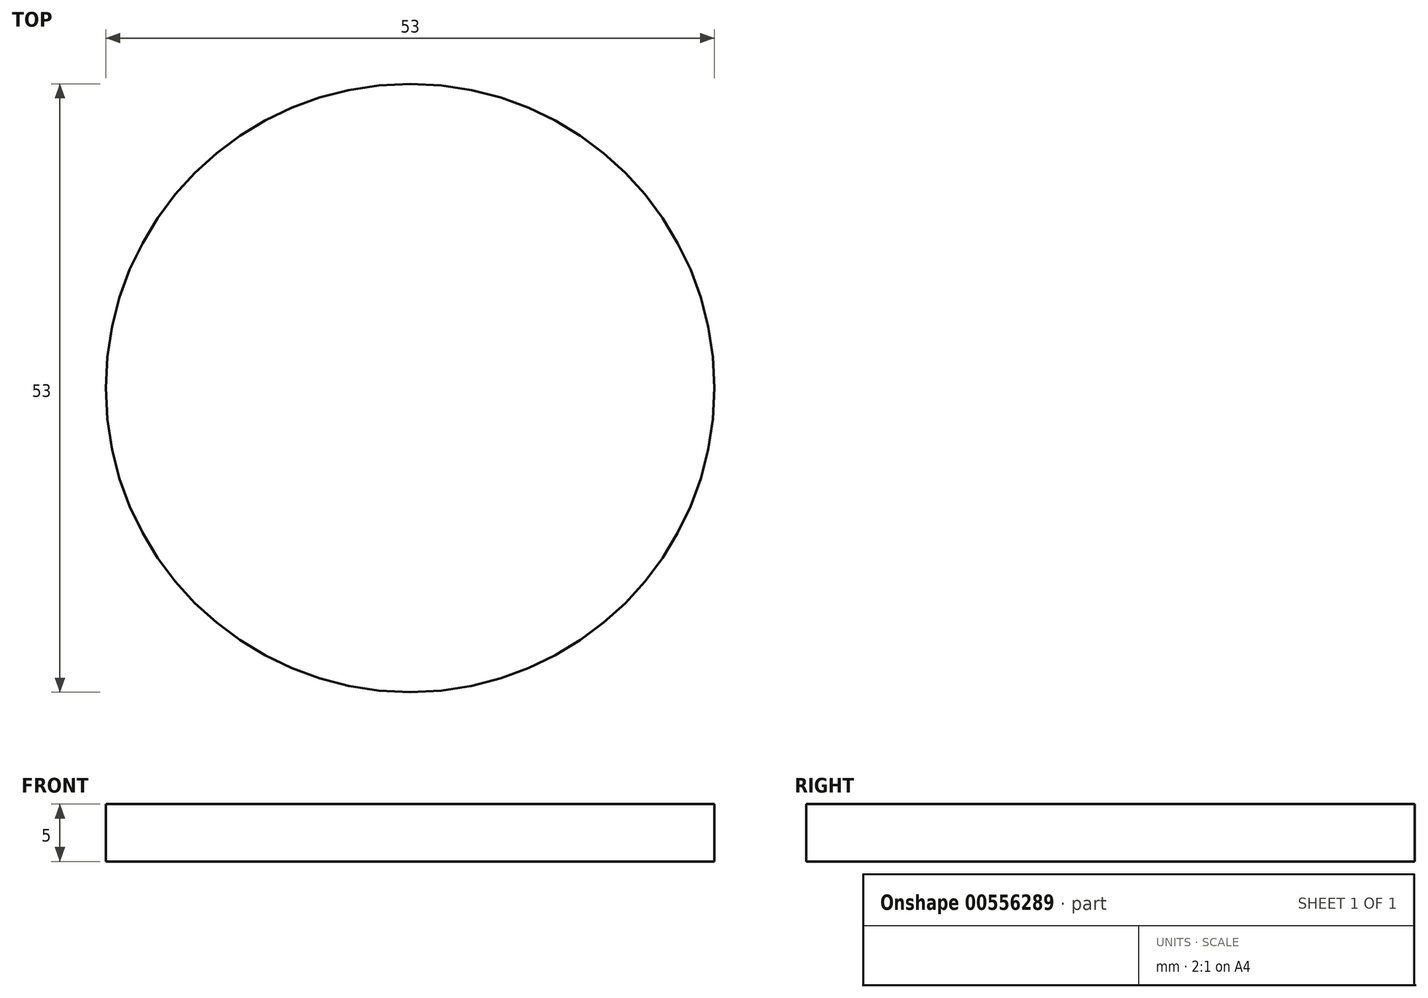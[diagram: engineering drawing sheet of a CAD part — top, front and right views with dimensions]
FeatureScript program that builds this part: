
annotation { "Feature Type Name" : "Feature", "Feature Type Description" : "" }
export const myFeature = defineFeature(function(context is Context, id is Id, definition is map)
    precondition{}
    {
        {
            var Q0;
            Q0=qCreatedBy(makeId("Top.planeOp"),FACE);
            var sketch = newSketch(context, id + "F0", { "sketchPlane" : qUnion([Q0])});
            skCircle(sketch, "E0", {"center": v(0, 0) * mm, "radius": 26.5 * mm});
            skSolve(sketch);
        }
        {
            var Q0;
            Q0=makeQuery(id+"F0.imprint","IMPRINT",FACE,{"disambiguationData":[TD([[makeQuery(id+"F0.imprint","IMPRINT",EDGE,{"derivedFrom":sQuery(id+"F0.wireOp",EDGE,"E0")}),1.0]])]});
            extrude(context, id + "F1", {"entities" : qUnion([Q0]), "depth" : 5 * mm, "offsetDistance" : 25 * mm});
        }
    });
